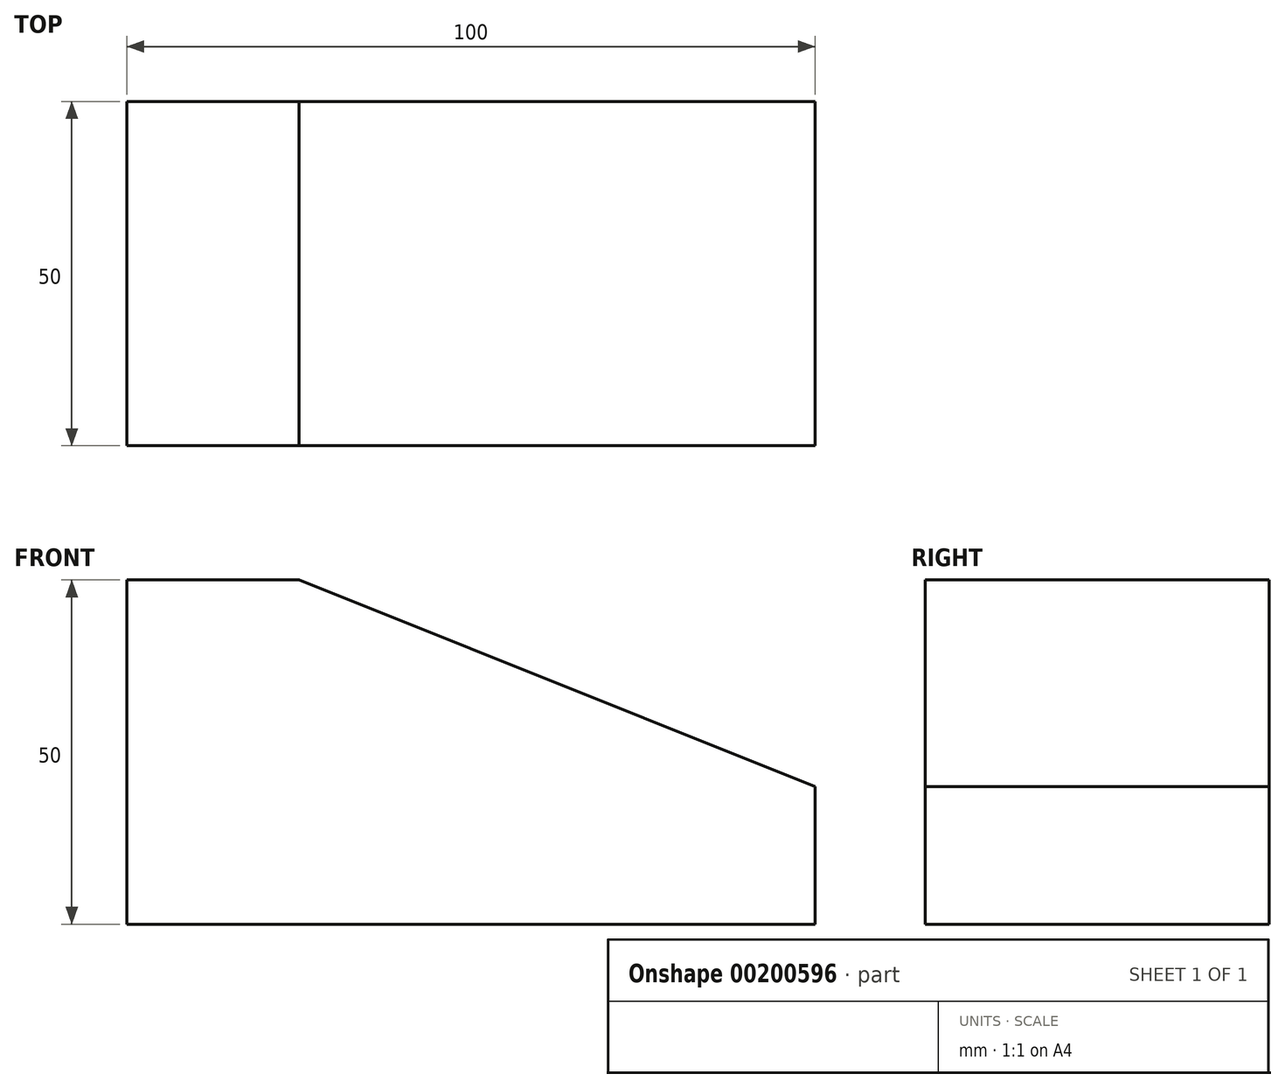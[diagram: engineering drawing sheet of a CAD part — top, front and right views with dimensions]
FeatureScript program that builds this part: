
annotation { "Feature Type Name" : "Feature", "Feature Type Description" : "" }
export const myFeature = defineFeature(function(context is Context, id is Id, definition is map)
    precondition{}
    {
        {
            var Q0;
            Q0=qCreatedBy(makeId("Front.planeOp"),FACE);
            var sketch = newSketch(context, id + "F0", { "sketchPlane" : qUnion([Q0])});
            skLineSegment(sketch, "E0.bottom", {"start": v(0, 0) * mm, "end": v(25, 0) * mm});
            skLineSegment(sketch, "E0.top", {"start": v(0, 50) * mm, "end": v(25, 50) * mm});
            skLineSegment(sketch, "E0.left", {"start": v(0, 0) * mm, "end": v(0, 50) * mm});
            skLineSegment(sketch, "E0.right", {"start": v(25, 0) * mm, "end": v(25, 50) * mm});
            skLineSegment(sketch, "E1", {"start": v(25, 50) * mm, "end": v(100, 20) * mm});
            skLineSegment(sketch, "E2", {"start": v(100, 20) * mm, "end": v(100, 0) * mm});
            skLineSegment(sketch, "E3", {"start": v(25, 0) * mm, "end": v(100, 0) * mm});
            skSolve(sketch);
        }
        {
            var Q0;
            Q0 = qSketchRegion(id + "F0", true);
            extrude(context, id + "F1", {"entities" : qUnion([Q0]), "depth" : 50 * mm});
        }
    });
